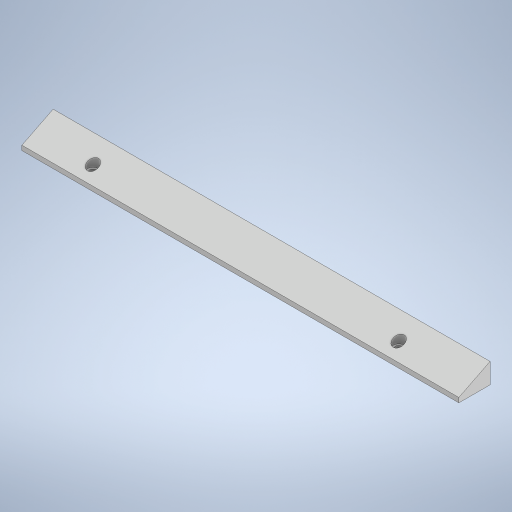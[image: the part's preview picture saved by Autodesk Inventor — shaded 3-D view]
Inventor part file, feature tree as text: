
AUTODESK INVENTOR PART (.ipt)
format: ipt  version: 2023 (Build 270158000, 158)  size: 267,776 bytes
history: native  units: in
note: dims shown in document units (in); Inventor stores cm internally (conversion verified against a paired STEP export)
features: sketch x6, extrude x5
ambient origin geometry x8: Origin, YZ Plane, XZ Plane, XY Plane, X Axis, Y Axis, Z Axis, Center Point
bodies: Solid1 (feature_tree)
feature tree (11):
  extrude  "Extrusion1"  Depth=0.3937in
  extrude  "Extrusion4"  Depth=0.1181in TaperAngle=0.0deg
  sketch  "Sketch7"  dims[d23=0.1693in d24=0.1693in]
  extrude  "Extrusion5"  Depth=0.1693in
  extrude  "Extrusion6"  Depth=0.1181in
  extrude  "Extrusion7"  Depth=0.3937in TaperAngle=0.0deg
  sketch  "Sketch1"  dims[d0=11.0236in d1=0.3937in]
  sketch  "Sketch6"  dims[d2=0.7874in d3=0.0in d21=0.1181in d22=0.0in]
  sketch  "Sketch8"  dims[d25=0.1181in d26=0.0in d27=0.2756in]
  sketch  "Sketch9"  dims[d28=0.2756in d29=0.3937in d30=0.0in]
  sketch  "Sketch10"  dims[d31=0.3937in d32=90.0deg d33=0.0in d34=0.0in]
